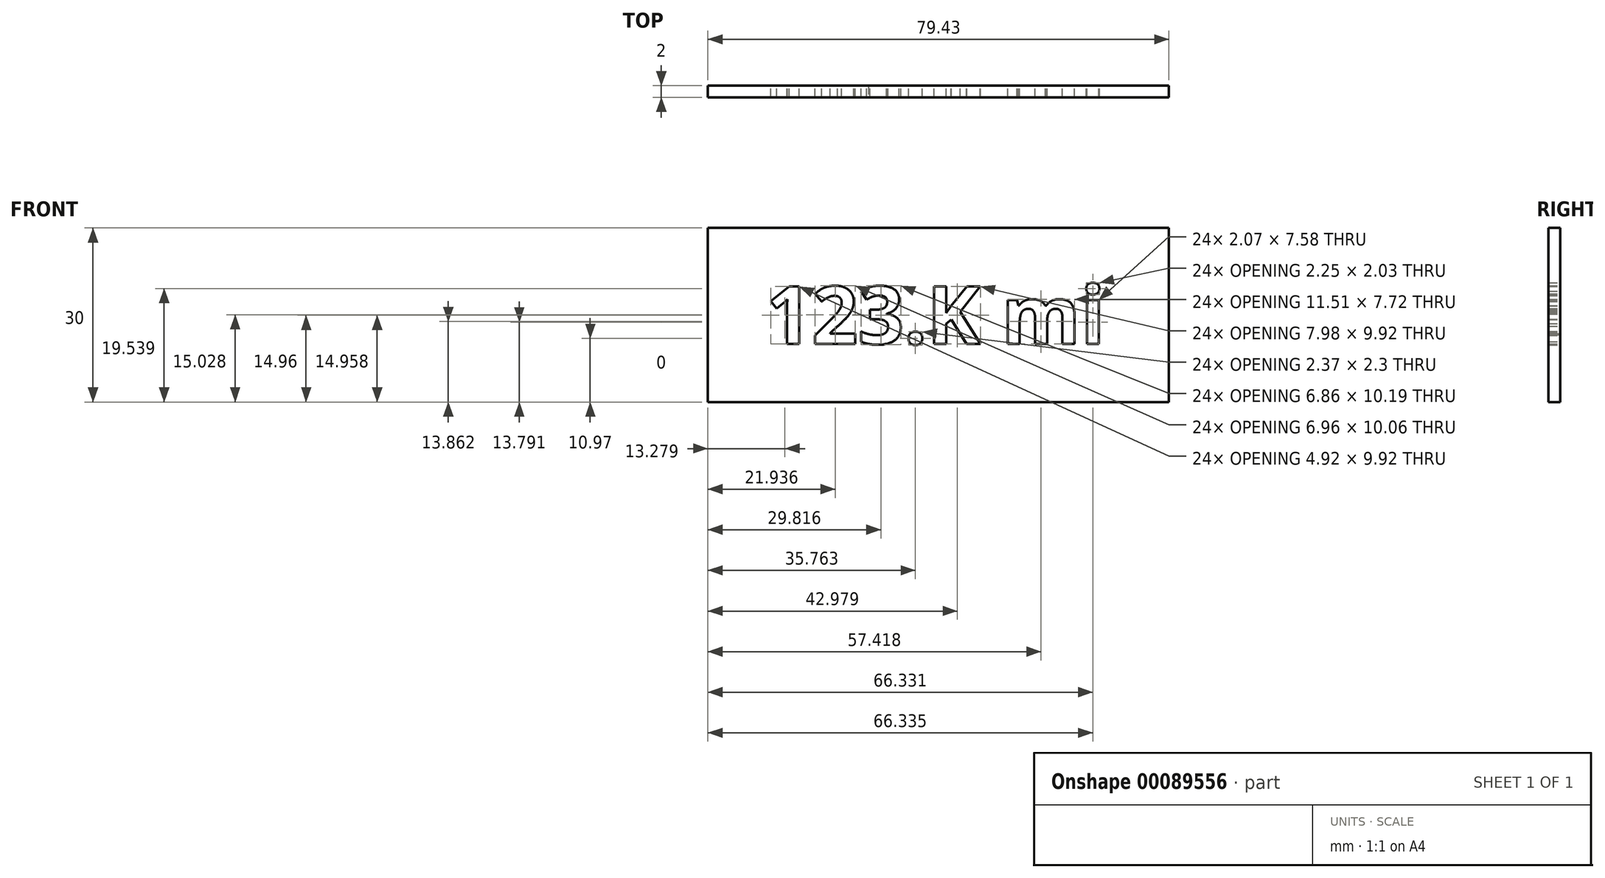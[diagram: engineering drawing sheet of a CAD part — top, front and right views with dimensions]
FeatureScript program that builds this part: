
annotation { "Feature Type Name" : "Feature", "Feature Type Description" : "" }
export const myFeature = defineFeature(function(context is Context, id is Id, definition is map)
    precondition{}
    {
        {
            var Q0;
            Q0=qCreatedBy(makeId("Front.planeOp"),FACE);
            var sketch = newSketch(context, id + "F0", { "sketchPlane" : qUnion([Q0])});
            skText(sketch, "E0", { "text": "123.K mi", "fontName": "OpenSans-Bold.ttf"});
            skLineSegment(sketch, "E1.bottom", {"start": v(-34.27, 16.4) * mm, "end": v(45.16, 16.4) * mm});
            skLineSegment(sketch, "E1.top", {"start": v(-34.27, -13.6) * mm, "end": v(45.16, -13.6) * mm});
            skLineSegment(sketch, "E1.left", {"start": v(-34.27, 16.4) * mm, "end": v(-34.27, -13.6) * mm});
            skLineSegment(sketch, "E1.right", {"start": v(45.16, 16.4) * mm, "end": v(45.16, -13.6) * mm});
            const initialGuessF0  = {"E0": [-0.02427, -0.0036, 1, 0, 0.01]};
            skSetInitialGuess(sketch, initialGuessF0);
            skSolve(sketch);
        }
        {
            var Q0;
            Q0=makeQuery(id+"F0.imprint","IMPRINT",FACE,{"disambiguationData":[TD([[makeQuery(id+"F0.imprint","IMPRINT",EDGE,{"derivedFrom":sQuery(id+"F0.wireOp",EDGE,"E0.sketch_text.stroke-0")}),1.0]])]});
            extrude(context, id + "F1", {"entities" : qUnion([Q0]), "depth" : 2 * mm});
        }
    });
